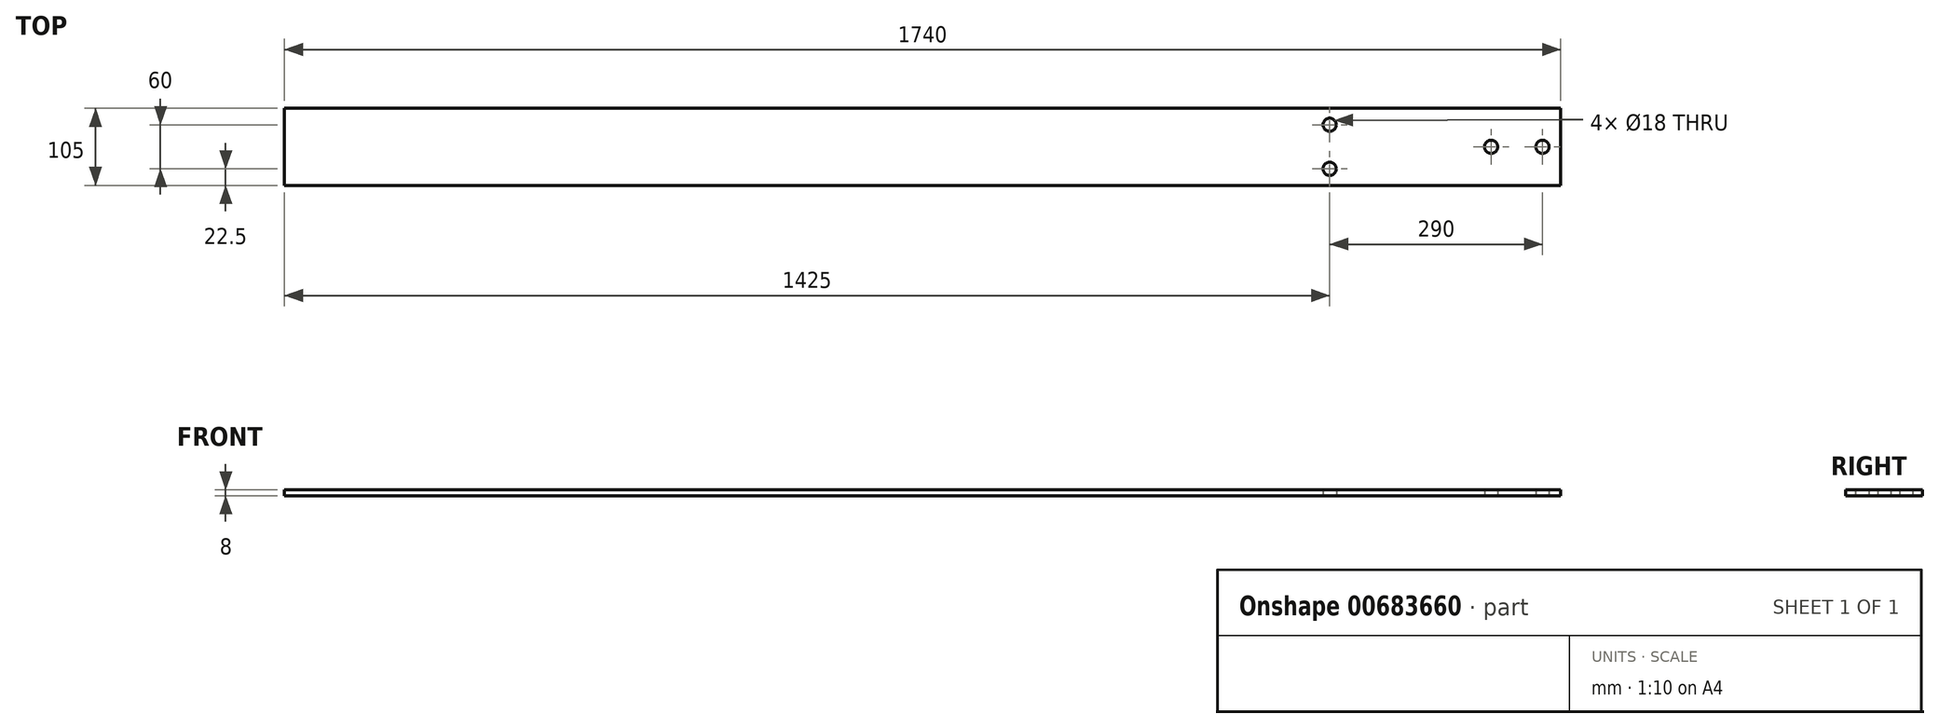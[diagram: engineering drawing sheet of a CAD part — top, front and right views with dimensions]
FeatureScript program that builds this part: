
annotation { "Feature Type Name" : "Feature", "Feature Type Description" : "" }
export const myFeature = defineFeature(function(context is Context, id is Id, definition is map)
    precondition{}
    {
        {
            var Q0;
            Q0=qCreatedBy(makeId("Top.planeOp"),FACE);
            var sketch = newSketch(context, id + "F0", { "sketchPlane" : qUnion([Q0])});
            skLineSegment(sketch, "E0.bottom", {"start": v(0, 0) * mm, "end": v(1740, 0) * mm});
            skLineSegment(sketch, "E0.top", {"start": v(0, 105) * mm, "end": v(1740, 105) * mm});
            skLineSegment(sketch, "E0.left", {"start": v(0, 0) * mm, "end": v(0, 105) * mm});
            skLineSegment(sketch, "E0.right", {"start": v(1740, 0) * mm, "end": v(1740, 105) * mm});
            skCircle(sketch, "E1", {"center": v(1715, 52.5) * mm, "radius": 9 * mm});
            skPoint(sketch, "E1.centerSnap0", {"position": v(1740, 52.5) * mm});
            skCircle(sketch, "E2", {"center": v(1645, 52.5) * mm, "radius": 9 * mm});
            skCircle(sketch, "E3", {"center": v(1425, 82.5) * mm, "radius": 9 * mm});
            skCircle(sketch, "E4", {"center": v(1425, 22.5) * mm, "radius": 9 * mm});
            skSolve(sketch);
        }
        {
            var Q0;
            Q0 = qSketchRegion(id + "F0", true);
            extrude(context, id + "F1", {"entities" : qUnion([Q0]), "depth" : 8 * mm, "offsetDistance" : 25 * mm});
        }
    });
